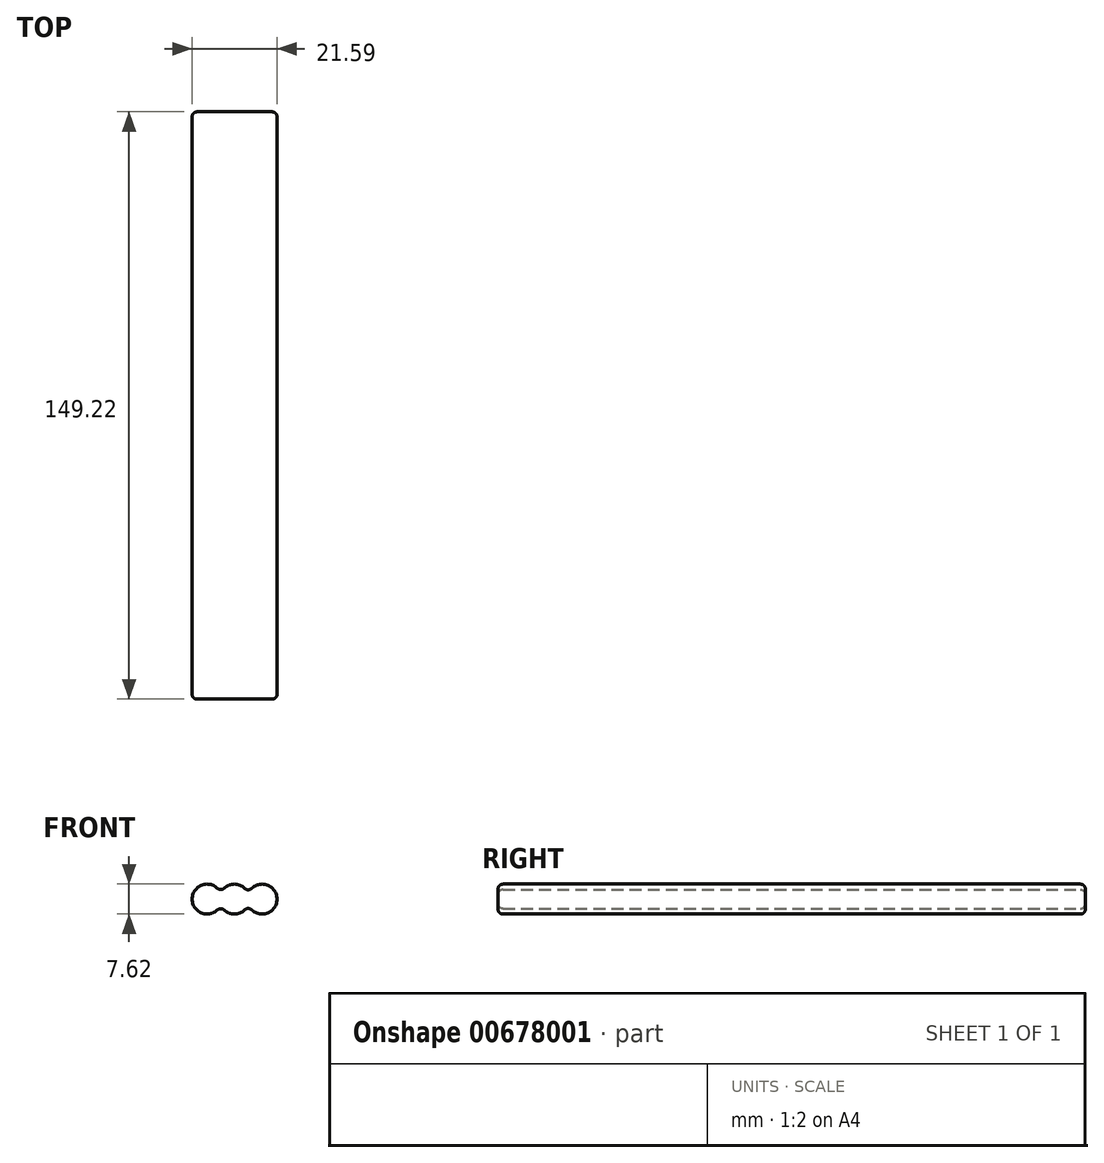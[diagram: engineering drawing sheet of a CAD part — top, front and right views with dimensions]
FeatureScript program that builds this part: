
annotation { "Feature Type Name" : "Feature", "Feature Type Description" : "" }
export const myFeature = defineFeature(function(context is Context, id is Id, definition is map)
    precondition{}
    {
        {
            var Q0;
            Q0=qCreatedBy(makeId("Front.planeOp"),FACE);
            var sketch = newSketch(context, id + "F0", { "sketchPlane" : qUnion([Q0])});
            skArc(sketch, "E0", {"start": v(-2.6, -2.79) * mm, "mid": v(0.03, -3.8) * mm, "end": v(2.64, -2.74) * mm});
            skArc(sketch, "E1", {"start": v(4.4, -2.74) * mm, "mid": v(10.86, 0) * mm, "end": v(4.4, 2.74) * mm});
            skArc(sketch, "E2", {"start": v(-4.32, 2.79) * mm, "mid": v(-10.73, 0) * mm, "end": v(-4.32, -2.79) * mm});
            skLineSegment(sketch, "E3", {"start": v(-6.92, 0) * mm, "end": v(7.05, 0) * mm, "construction": true});
            skArc(sketch, "E4.trimOffspring", {"start": v(2.64, 2.74) * mm, "mid": v(0.03, 3.8) * mm, "end": v(-2.6, 2.79) * mm});
            skPoint(sketch, "E5.visualSharp", {"position": v(-3.46, 1.6) * mm});
            skArc(sketch, "E5.filletArc", {"start": v(-4.32, 2.79) * mm, "mid": v(-3.46, 2.45) * mm, "end": v(-2.6, 2.79) * mm});
            skPoint(sketch, "E6.visualSharp", {"position": v(-3.46, -1.6) * mm});
            skArc(sketch, "E6.filletArc", {"start": v(-2.6, -2.79) * mm, "mid": v(-3.46, -2.45) * mm, "end": v(-4.32, -2.79) * mm});
            skPoint(sketch, "E7.visualSharp", {"position": v(3.53, -1.45) * mm});
            skArc(sketch, "E7.filletArc", {"start": v(4.4, -2.74) * mm, "mid": v(3.53, -2.39) * mm, "end": v(2.64, -2.74) * mm});
            skPoint(sketch, "E8.visualSharp", {"position": v(3.53, 1.45) * mm});
            skArc(sketch, "E8.filletArc", {"start": v(2.64, 2.74) * mm, "mid": v(3.53, 2.39) * mm, "end": v(4.4, 2.74) * mm});
            skSolve(sketch);
        }
        {
            var Q0;
            Q0=makeQuery(id+"F0.imprint","IMPRINT",FACE,{"disambiguationData":[TD([[makeQuery(id+"F0.imprint","IMPRINT",EDGE,{"derivedFrom":sQuery(id+"F0.wireOp",EDGE,"E0")}),1.0]])]});
            extrude(context, id + "F1", {"entities" : qUnion([Q0]), "depth" : 149.22 * mm, "offsetDistance" : 25.4 * mm, "symmetric" : true});
        }
        {
            var Q0;
            Q0=makeQuery(id+"F1.opExtrude","CAP_EDGE",EDGE,{"disambiguationData":[OSD([sQuery(id+"F0.wireOp",EDGE,"E0")])],"isStart":false});
            var Q1;
            Q1=makeQuery(id+"F1.opExtrude","CAP_EDGE",EDGE,{"disambiguationData":[OSD([sQuery(id+"F0.wireOp",EDGE,"E1")])],"isStart":true});
            fillet(context, id + "F2", {"entities" : qUnion([Q0, Q1]), "radius" : 1.27 * mm, "tangentPropagation" : true, "allowEdgeOverflow" : false});
        }
    });
